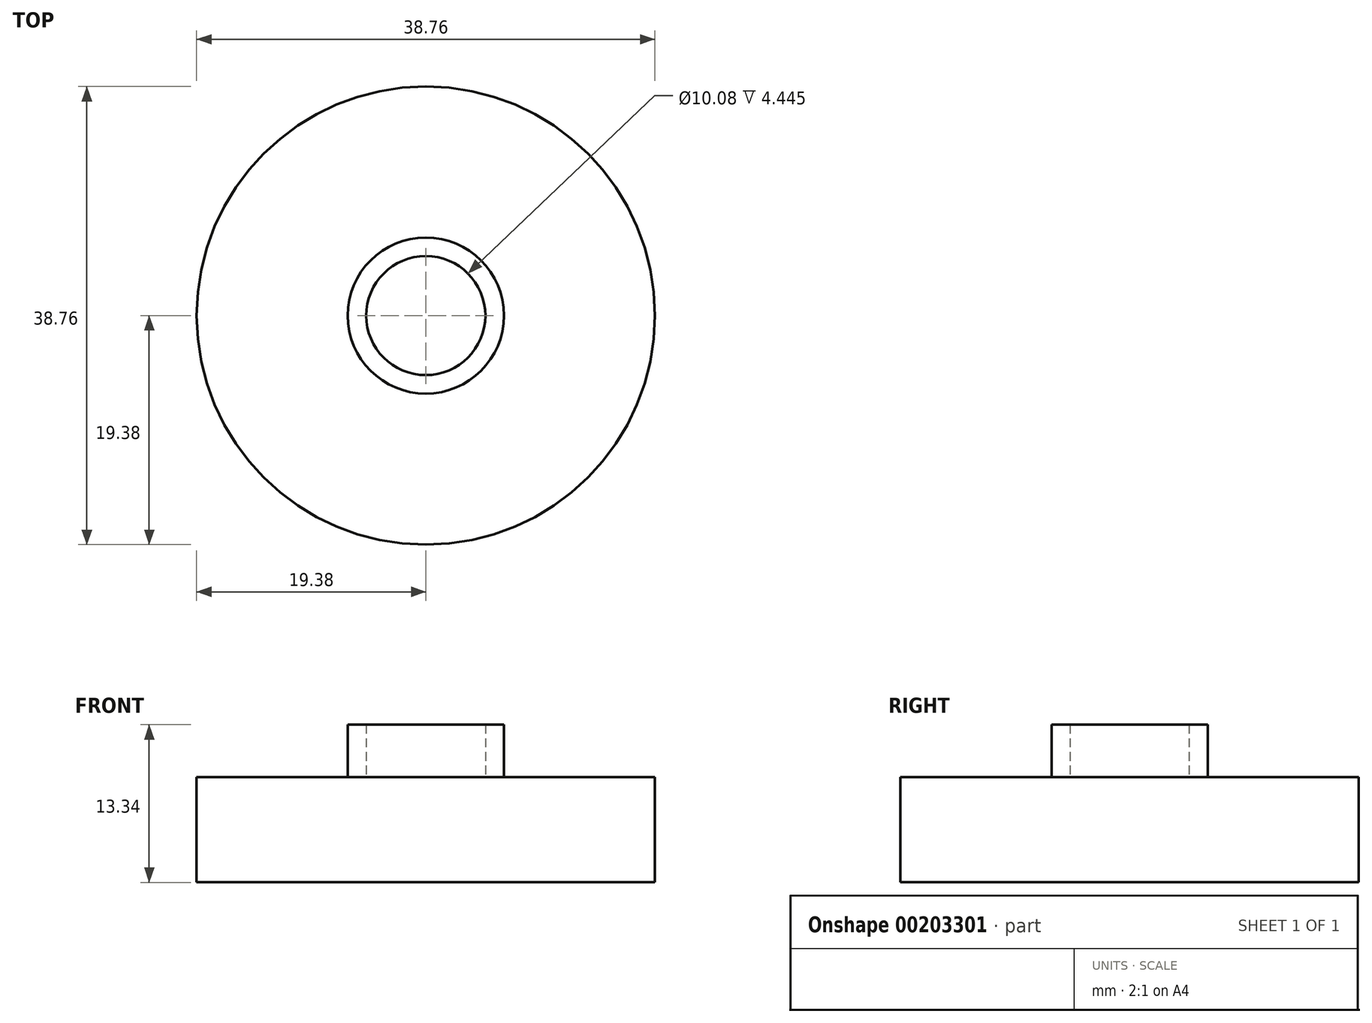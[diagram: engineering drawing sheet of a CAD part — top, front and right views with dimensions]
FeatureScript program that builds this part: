
annotation { "Feature Type Name" : "Feature", "Feature Type Description" : "" }
export const myFeature = defineFeature(function(context is Context, id is Id, definition is map)
    precondition{}
    {
        {
            var Q0;
            Q0=qCreatedBy(makeId("Top.planeOp"),FACE);
            var sketch = newSketch(context, id + "F3", { "sketchPlane" : qUnion([Q0])});
            skCircle(sketch, "E0", {"center": v(0, 0) * mm, "radius": 5.04 * mm});
            skCircle(sketch, "E1", {"center": v(0, 0) * mm, "radius": 6.6 * mm});
            skCircle(sketch, "E2", {"center": v(0, 0) * mm, "radius": 18.92 * mm});
            skSolve(sketch);
        }
        {
            var Q0;
            Q0=makeQuery(id+"F3.imprint","IMPRINT",FACE,{"disambiguationData":[TD([[makeQuery(id+"F3.imprint","IMPRINT",EDGE,{"derivedFrom":sQuery(id+"F3.wireOp",EDGE,"E0")}),-1.0]])]});
            extrude(context, id + "F0", {"entities" : qUnion([Q0]), "depth" : 8.9 * mm});
        }
        {
            var Q0;
            Q0=qCreatedBy(makeId("Top.planeOp"),FACE);
            var sketch = newSketch(context, id + "F4", { "sketchPlane" : qUnion([Q0])});
            skCircle(sketch, "E3", {"center": v(0, 0) * mm, "radius": 11.15 * mm});
            skSolve(sketch);
        }
        {
            var Q0;
            Q0=makeQuery(id+"F4.imprint","IMPRINT",FACE,{"disambiguationData":[TD([[makeQuery(id+"F4.imprint","IMPRINT",EDGE,{"derivedFrom":sQuery(id+"F4.wireOp",EDGE,"E3")}),1.0]])]});
            extrude(context, id + "F5", {"entities" : qUnion([Q0]), "operationType" : NewBodyOperationType.ADD, "depth" : 2.54 * mm});
        }
        {
            var Q0;
            Q0=qCreatedBy(makeId("Top.planeOp"),FACE);
            var sketch = newSketch(context, id + "F1", { "sketchPlane" : qUnion([Q0])});
            skCircle(sketch, "E4", {"center": v(0, 0) * mm, "radius": 19.38 * mm});
            skSolve(sketch);
        }
        {
            var Q0;
            Q0=makeQuery(id+"F1.imprint","IMPRINT",FACE,{"disambiguationData":[TD([[makeQuery(id+"F1.imprint","IMPRINT",EDGE,{"derivedFrom":sQuery(id+"F1.wireOp",EDGE,"E4")}),1.0]])]});
            extrude(context, id + "F2", {"entities" : qUnion([Q0]), "operationType" : NewBodyOperationType.ADD, "depth" : 4.44 * mm});
        }
        {
            var Q0;
            Q0=makeQuery(id+"F2.boolean.opBoolean","MERGE",FACE,{"derivedFrom":[makeQuery(id+"F5.boolean.opBoolean","MERGE",FACE,{"derivedFrom":[makeQuery(id+"F0.opExtrude","CAP_FACE",FACE,{"disambiguationData":[OSD([sQuery(id+"F3.wireOp",EDGE,"E0"),sQuery(id+"F3.wireOp",EDGE,"E1")])],"isStart":true}),makeQuery(id+"F5.opExtrude","CAP_FACE",FACE,{"disambiguationData":[OSD([sQuery(id+"F4.wireOp",EDGE,"E3")])],"isStart":true})]}),makeQuery(id+"F2.opExtrude","CAP_FACE",FACE,{"disambiguationData":[OSD([sQuery(id+"F1.wireOp",EDGE,"E4")])],"isStart":true})]});
            extrude(context, id + "F6", {"entities" : qUnion([Q0]), "operationType" : NewBodyOperationType.ADD, "depth" : 4.44 * mm});
        }
    });
